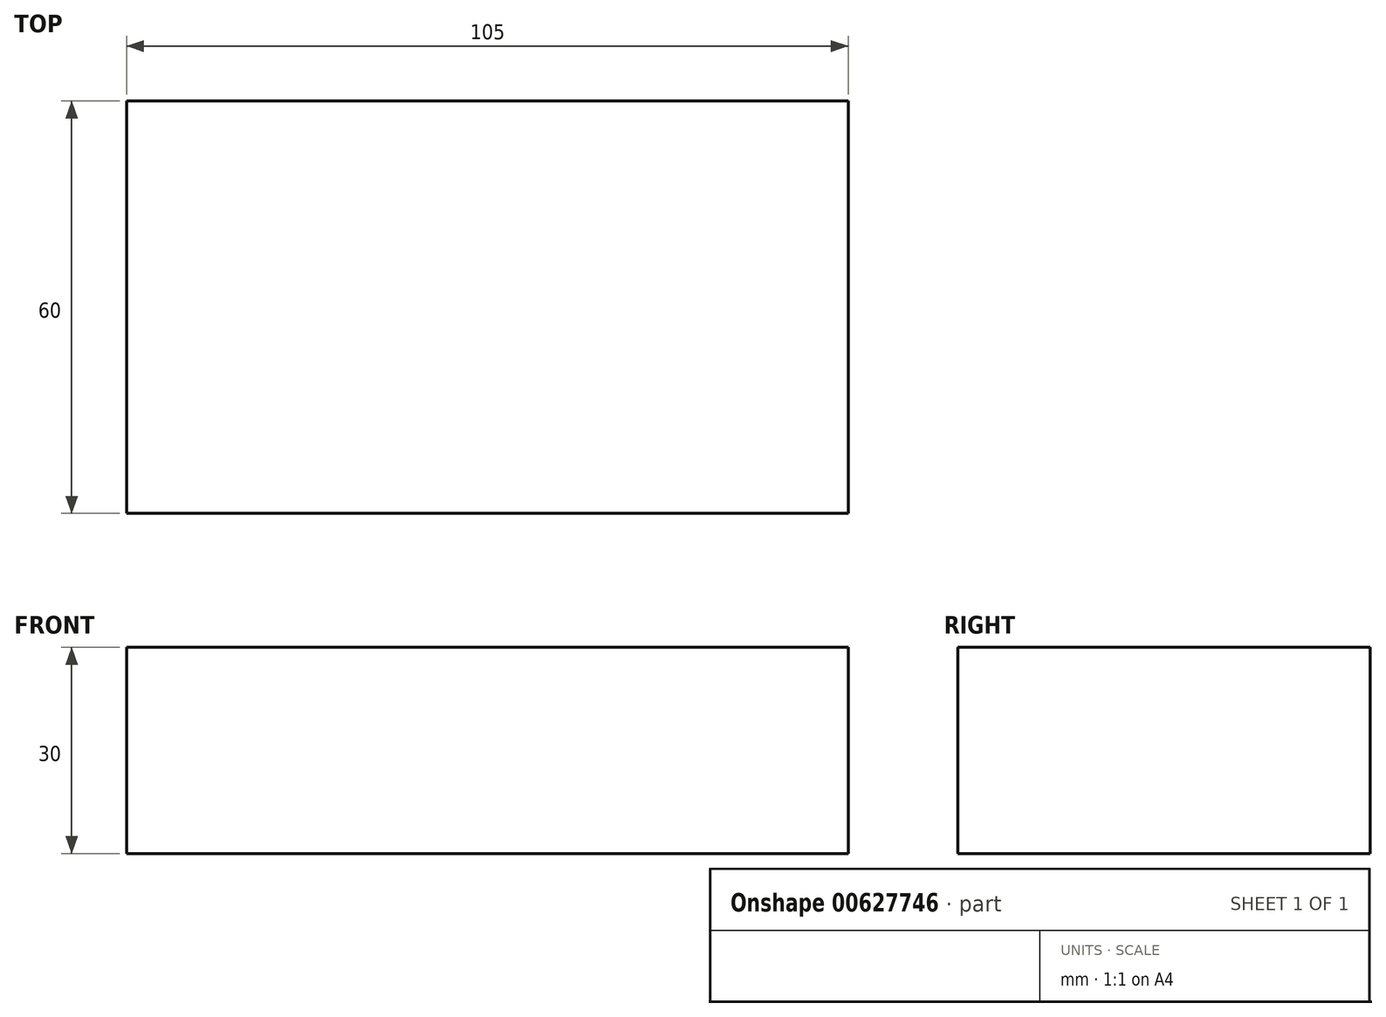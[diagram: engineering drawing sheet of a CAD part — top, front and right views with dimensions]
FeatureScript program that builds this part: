
annotation { "Feature Type Name" : "Feature", "Feature Type Description" : "" }
export const myFeature = defineFeature(function(context is Context, id is Id, definition is map)
    precondition{}
    {
        {
            var Q0;
            Q0=qCreatedBy(makeId("Front.planeOp"),FACE);
            var sketch = newSketch(context, id + "F0", { "sketchPlane" : qUnion([Q0])});
            skLineSegment(sketch, "E0.bottom", {"start": v(-52.5, -15) * mm, "end": v(52.5, -15) * mm});
            skLineSegment(sketch, "E0.top", {"start": v(-52.5, 15) * mm, "end": v(52.5, 15) * mm});
            skLineSegment(sketch, "E0.left", {"start": v(-52.5, -15) * mm, "end": v(-52.5, 15) * mm});
            skLineSegment(sketch, "E0.right", {"start": v(52.5, -15) * mm, "end": v(52.5, 15) * mm});
            skPoint(sketch, "E0.middle", {"position": v(0, 0) * mm});
            skSolve(sketch);
        }
        {
            var Q0;
            Q0 = qSketchRegion(id + "F0", true);
            extrude(context, id + "F1", {"entities" : qUnion([Q0]), "depth" : 60 * mm, "offsetDistance" : 25 * mm});
        }
    });
